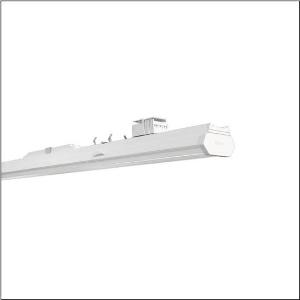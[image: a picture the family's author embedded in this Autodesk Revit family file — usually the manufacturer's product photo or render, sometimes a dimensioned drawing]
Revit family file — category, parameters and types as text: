
# Revit family: licross_r__11_protected_mo_51tp127n485g_ff31
name_source: partatom
category: Lighting Fixtures
units: mm (PartAtom-declared; Revit-internal decimal feet)

## family parameters
Cut with Voids When Loaded = No
Host = Face
Light Source = No
Part Type = Normal
Room Calculation Point = No
Round Connector Dimension = Use Diameter
Shared = No

## types (1)
- Licross® 11 Protected MO (1 x LED, 8720 lm, 48.6 W, 4000K)
    Apparent Load = 49 VA
    CIE Flux Codes = 73 92 98 99 100
    Color Rendering = 80
    Color Temperature = 4000K
    Default Elevation = 1800 mm
    Description = Licross® 11 Protected MO, luminaire insert, of sheet steel, galvanised, coil coated, white, length: 1.500mm, width: 90mm, height: 101mm, LED rated luminous flux: 8.720lm, light colour: 840, control gear: ON/OFF, with plug, 3-pole, with phase selection, mains connection: 220..240V, AC, 50/60Hz, rated input power: 49W, halogen-free wiring, primary light control with lens, of plastic, primary optical cover: cover, of PMMA, light emission: direct distribution, primary light characteristic: symmetric, protection rating (complete): IP64, insulation class (complete): insulation class I (protective earthing), certification: CE, ENEC, VDE, UKCA, protection symbol: D if used in an environment with conductive dust loads with corresponding accessories, impact resistance: IK06, permissible ambient temperature for indoor applications: -25..+35°C, corresponds to IFS (International Featured Standards) requirements for safety and quality in the food industry, reducing of maximum allowable ambient temperature of 5°C with ceiling mounting, LABS conformity tested according to VDMA 24364:2018-05, packaging unit: 1 piece
    Height = 92 mm
    Lamp = 1 x LED
    Lamp Light Flux = 8720 lm
    Lamp Power = 48.6 W
    Lamp count = 1
    Length = 1500 mm
    Luminous efficacy = 179 lm/W
    Manufacturer = Siteco
    ModVariant = No
    Model = 51TP127N485G
    Mounting Place = Ceiling
    Mounting Type = Pendant
    Number of Poles = 1
    OnlyDefault = Yes
    Power Factor = 1
    Product Name = Licross® 11 Protected MO
    Product group = luminaire insert
    ProductGroupID = 901
    Protection Class = Protection class I
    Protection Degree = IP 64
    RLX_Detail_Level = 1
    RLX_Emergency_Light_Flux = 0 lm
    RLX_Emergency_Type = 0
    RLX_Emergency_Type_DB = No
    RlxData = <blob elided: 20673 chars, md5=c1d94270>
    Socket = socket
    Standby Power = 0 W
    System Light Flux = 8720 lm
    System Power = 49 W
    Type Comments = Product without accessories
    Type Image = l_1256148.jpg
    URL = http://relux.com
    VarID = ---
    Voltage = 0 V
    Weight = 0.00 kg
    Width = 88 mm

## geometry (parser evidence)
native form markers: Blend x4, Sweep x12
no freeform markers — native parametric forms only
